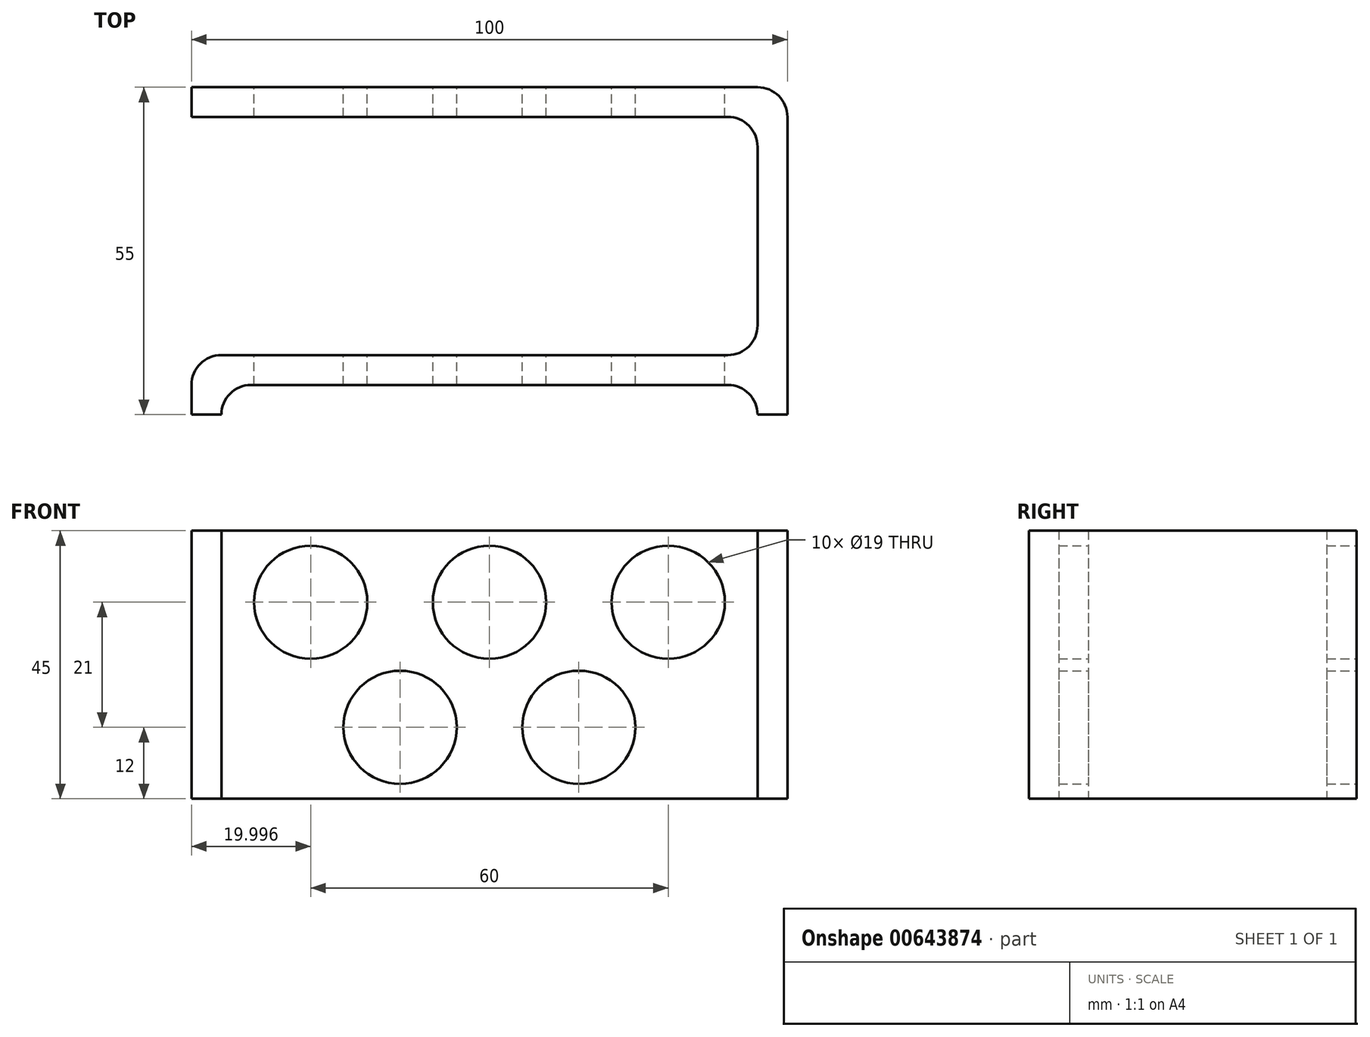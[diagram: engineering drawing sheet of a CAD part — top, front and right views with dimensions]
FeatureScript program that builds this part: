
annotation { "Feature Type Name" : "Feature", "Feature Type Description" : "" }
export const myFeature = defineFeature(function(context is Context, id is Id, definition is map)
    precondition{}
    {
        {
            var Q0;
            Q0=qCreatedBy(makeId("Top.planeOp"),FACE);
            var sketch = newSketch(context, id + "F0", { "sketchPlane" : qUnion([Q0])});
            skLineSegment(sketch, "E0.bottom", {"start": v(-34.12, 17.55) * mm, "end": v(65.88, 17.55) * mm});
            skLineSegment(sketch, "E0.top", {"start": v(-29.12, -32.45) * mm, "end": v(60.88, -32.45) * mm});
            skLineSegment(sketch, "E0.right", {"start": v(65.88, 17.55) * mm, "end": v(65.88, -32.45) * mm});
            skLineSegment(sketch, "E1.bottom", {"start": v(-34.12, 12.55) * mm, "end": v(60.88, 12.55) * mm});
            skLineSegment(sketch, "E1.top", {"start": v(-34.12, -27.45) * mm, "end": v(60.88, -27.45) * mm});
            skLineSegment(sketch, "E1.right", {"start": v(60.88, 12.55) * mm, "end": v(60.88, -27.45) * mm});
            skLineSegment(sketch, "E2", {"start": v(-34.12, 12.55) * mm, "end": v(-34.12, 17.55) * mm});
            skLineSegment(sketch, "E3", {"start": v(-34.12, 17.55) * mm, "end": v(-34.12, 12.55) * mm});
            skLineSegment(sketch, "E4.trimOffspring", {"start": v(-34.12, -27.45) * mm, "end": v(-34.12, -32.45) * mm});
            skLineSegment(sketch, "E5.top", {"start": v(-34.12, -37.45) * mm, "end": v(-29.12, -37.45) * mm});
            skLineSegment(sketch, "E5.left", {"start": v(-34.12, -32.45) * mm, "end": v(-34.12, -37.45) * mm});
            skLineSegment(sketch, "E5.right", {"start": v(-29.12, -32.45) * mm, "end": v(-29.12, -37.45) * mm});
            skLineSegment(sketch, "E6.top", {"start": v(65.88, -37.45) * mm, "end": v(60.88, -37.45) * mm});
            skLineSegment(sketch, "E6.left", {"start": v(65.88, -32.45) * mm, "end": v(65.88, -37.45) * mm});
            skLineSegment(sketch, "E6.right", {"start": v(60.88, -32.45) * mm, "end": v(60.88, -37.45) * mm});
            skSolve(sketch);
        }
        {
            var Q0;
            Q0=makeQuery(id+"F0.imprint","IMPRINT",FACE,{"disambiguationData":[TD([[makeQuery(id+"F0.imprint","IMPRINT",EDGE,{"derivedFrom":sQuery(id+"F0.wireOp",EDGE,"E0.bottom")}),-1.0]])]});
            extrude(context, id + "F1", {"entities" : qUnion([Q0]), "depth" : 45 * mm, "offsetDistance" : 25 * mm});
        }
        {
            var Q0;
            Q0=makeQuery(id+"F1.opExtrude","SWEPT_EDGE",EDGE,{"disambiguationData":[OSD([sQuery(id+"F0.wireOp",EDGE,"E1.bottom"),sQuery(id+"F0.wireOp",EDGE,"E1.right")])]});
            var Q1;
            Q1=makeQuery(id+"F1.opExtrude","SWEPT_EDGE",EDGE,{"disambiguationData":[OSD([sQuery(id+"F0.wireOp",EDGE,"E1.top"),sQuery(id+"F0.wireOp",EDGE,"E1.right")])]});
            var Q2;
            Q2=makeQuery(id+"F1.opExtrude","SWEPT_EDGE",EDGE,{"disambiguationData":[OSD([sQuery(id+"F0.wireOp",EDGE,"E0.bottom"),sQuery(id+"F0.wireOp",EDGE,"E0.right")])]});
            var Q3;
            Q3=makeQuery(id+"F1.opExtrude","SWEPT_EDGE",EDGE,{"disambiguationData":[OSD([sQuery(id+"F0.wireOp",EDGE,"E0.top"),sQuery(id+"F0.wireOp",EDGE,"E6.right")])]});
            var Q4;
            Q4=makeQuery(id+"F1.opExtrude","SWEPT_EDGE",EDGE,{"disambiguationData":[OSD([sQuery(id+"F0.wireOp",EDGE,"E0.top"),sQuery(id+"F0.wireOp",EDGE,"E5.right")])]});
            var Q5;
            Q5=makeQuery(id+"F1.opExtrude","SWEPT_EDGE",EDGE,{"disambiguationData":[OSD([sQuery(id+"F0.wireOp",EDGE,"E1.top"),sQuery(id+"F0.wireOp",EDGE,"E4.trimOffspring")])]});
            fillet(context, id + "F2", {"entities" : qUnion([Q0, Q1, Q2, Q3, Q4, Q5]), "radius" : 5 * mm, "tangentPropagation" : true, "allowEdgeOverflow" : false});
        }
        {
            var Q0;
            Q0=makeQuery(id+"F1.opExtrude","SWEPT_FACE",FACE,{"disambiguationData":[OSD([sQuery(id+"F0.wireOp",EDGE,"E0.bottom")])]});
            var sketch = newSketch(context, id + "F3", { "sketchPlane" : qUnion([Q0])});
            skCircle(sketch, "E7", {"center": v(-45.88, 33) * mm, "radius": 9.5 * mm});
            skCircle(sketch, "E8", {"center": v(-0.88, 12) * mm, "radius": 9.5 * mm});
            skCircle(sketch, "E9", {"center": v(14.12, 33) * mm, "radius": 9.5 * mm});
            skCircle(sketch, "E10", {"center": v(-30.88, 12) * mm, "radius": 9.5 * mm});
            skCircle(sketch, "E11", {"center": v(-15.88, 33) * mm, "radius": 9.5 * mm});
            skSolve(sketch);
        }
        {
            var Q0;
            Q0 = qSketchRegion(id + "F3", true);
            extrude(context, id + "F4", {"entities" : qUnion([Q0]), "operationType" : NewBodyOperationType.REMOVE, "oppositeDirection" : true, "depth" : 80 * mm, "offsetDistance" : 25 * mm});
        }
    });
